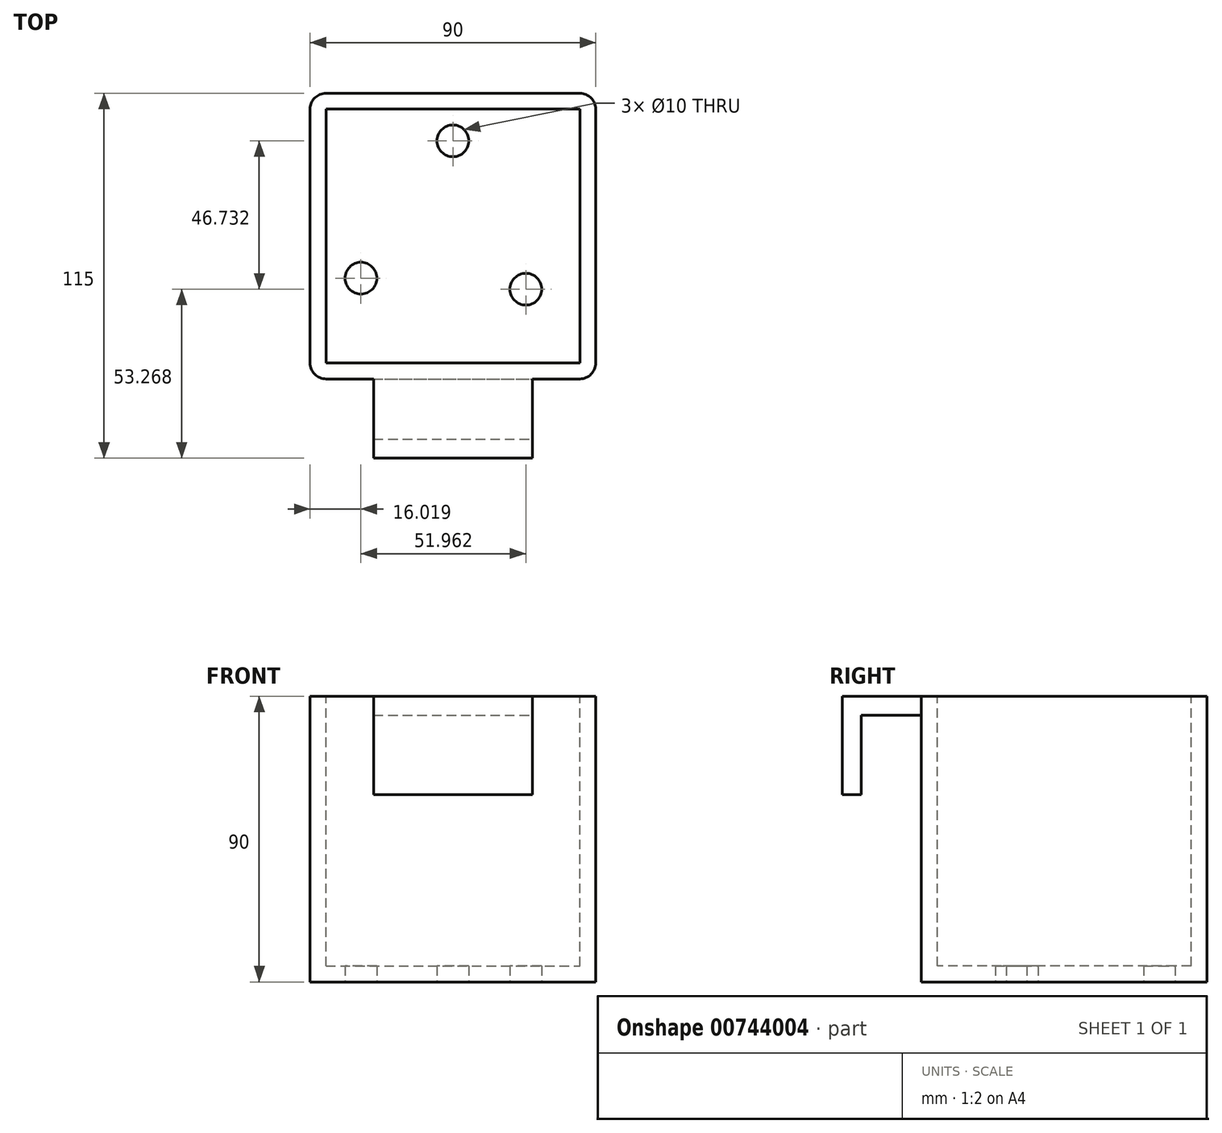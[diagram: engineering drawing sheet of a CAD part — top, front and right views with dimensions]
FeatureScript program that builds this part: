
annotation { "Feature Type Name" : "Feature", "Feature Type Description" : "" }
export const myFeature = defineFeature(function(context is Context, id is Id, definition is map)
    precondition{}
    {
        {
            var Q0;
            Q0=qCreatedBy(makeId("Top.planeOp"),FACE);
            var sketch = newSketch(context, id + "F0", { "sketchPlane" : qUnion([Q0])});
            skLineSegment(sketch, "E0.bottom", {"start": v(0, 0) * mm, "end": v(90, 0) * mm});
            skLineSegment(sketch, "E0.top", {"start": v(0, 90) * mm, "end": v(90, 90) * mm});
            skLineSegment(sketch, "E0.left", {"start": v(0, 0) * mm, "end": v(0, 90) * mm});
            skLineSegment(sketch, "E0.right", {"start": v(90, 0) * mm, "end": v(90, 90) * mm});
            skCircle(sketch, "E1", {"center": v(45, 75) * mm, "radius": 5 * mm});
            skCircle(sketch, "E2.1.0", {"center": v(16.02, 31.73) * mm, "radius": 5 * mm});
            skCircle(sketch, "E2.2.0", {"center": v(67.98, 28.27) * mm, "radius": 5 * mm});
            skPoint(sketch, "E2.center", {"position": v(43, 45) * mm});
            skSolve(sketch);
        }
        {
            var Q0;
            Q0=makeQuery(id+"F0.imprint","IMPRINT",FACE,{"disambiguationData":[TD([[makeQuery(id+"F0.imprint","IMPRINT",EDGE,{"derivedFrom":sQuery(id+"F0.wireOp",EDGE,"E0.bottom")}),1.0]])]});
            extrude(context, id + "F1", {"entities" : qUnion([Q0]), "depth" : 90 * mm, "offsetDistance" : 25 * mm});
        }
        {
            var Q0;
            Q0=makeQuery(id+"F1.opExtrude","SWEPT_EDGE",EDGE,{"disambiguationData":[OSD([sQuery(id+"F0.wireOp",EDGE,"E0.bottom"),sQuery(id+"F0.wireOp",EDGE,"E0.right")])]});
            var Q1;
            Q1=makeQuery(id+"F1.opExtrude","SWEPT_EDGE",EDGE,{"disambiguationData":[OSD([sQuery(id+"F0.wireOp",EDGE,"E0.top"),sQuery(id+"F0.wireOp",EDGE,"E0.right")])]});
            var Q2;
            Q2=makeQuery(id+"F1.opExtrude","SWEPT_EDGE",EDGE,{"disambiguationData":[OSD([sQuery(id+"F0.wireOp",EDGE,"E0.bottom"),sQuery(id+"F0.wireOp",EDGE,"E0.left")])]});
            var Q3;
            Q3=makeQuery(id+"F1.opExtrude","SWEPT_EDGE",EDGE,{"disambiguationData":[OSD([sQuery(id+"F0.wireOp",EDGE,"E0.top"),sQuery(id+"F0.wireOp",EDGE,"E0.left")])]});
            fillet(context, id + "F2", {"entities" : qUnion([Q0, Q1, Q2, Q3]), "radius" : 5 * mm, "tangentPropagation" : true, "allowEdgeOverflow" : false});
        }
        {
            var Q0;
            Q0=makeQuery(id+"F1.opExtrude","CAP_FACE",FACE,{"disambiguationData":[OSD([sQuery(id+"F0.wireOp",EDGE,"E0.bottom"),sQuery(id+"F0.wireOp",EDGE,"E0.top"),sQuery(id+"F0.wireOp",EDGE,"E0.left"),sQuery(id+"F0.wireOp",EDGE,"E0.right"),sQuery(id+"F0.wireOp",EDGE,"E1"),sQuery(id+"F0.wireOp",EDGE,"E2.1.0"),sQuery(id+"F0.wireOp",EDGE,"E2.2.0")])],"isStart":false});
            var sketch = newSketch(context, id + "F3", { "sketchPlane" : qUnion([Q0])});
            skLineSegment(sketch, "E3.bottom", {"start": v(5, 85) * mm, "end": v(85, 85) * mm});
            skLineSegment(sketch, "E3.top", {"start": v(5, 5) * mm, "end": v(85, 5) * mm});
            skLineSegment(sketch, "E3.left", {"start": v(5, 85) * mm, "end": v(5, 5) * mm});
            skLineSegment(sketch, "E3.right", {"start": v(85, 85) * mm, "end": v(85, 5) * mm});
            skSolve(sketch);
        }
        {
            var Q0;
            Q0 = qSketchRegion(id + "F3", true);
            extrude(context, id + "F4", {"entities" : qUnion([Q0]), "operationType" : NewBodyOperationType.REMOVE, "oppositeDirection" : true, "depth" : 85 * mm, "offsetDistance" : 25 * mm});
        }
        {
            var Q0;
            Q0=makeQuery(id+"F1.opExtrude","SWEPT_FACE",FACE,{"disambiguationData":[OSD([sQuery(id+"F0.wireOp",EDGE,"E0.bottom")])]});
            var sketch = newSketch(context, id + "F5", { "sketchPlane" : qUnion([Q0])});
            skLineSegment(sketch, "E4.bottom", {"start": v(20, 90) * mm, "end": v(70, 90) * mm});
            skLineSegment(sketch, "E4.top", {"start": v(20, 84) * mm, "end": v(70, 84) * mm});
            skLineSegment(sketch, "E4.left", {"start": v(20, 90) * mm, "end": v(20, 84) * mm});
            skLineSegment(sketch, "E4.right", {"start": v(70, 90) * mm, "end": v(70, 84) * mm});
            skSolve(sketch);
        }
        {
            var Q0;
            Q0 = qSketchRegion(id + "F5", true);
            extrude(context, id + "F6", {"entities" : qUnion([Q0]), "operationType" : NewBodyOperationType.ADD, "depth" : 25 * mm, "offsetDistance" : 25 * mm});
        }
        {
            var Q0;
            Q0=makeQuery(id+"F6.opExtrude","SWEPT_FACE",FACE,{"disambiguationData":[OSD([sQuery(id+"F5.wireOp",EDGE,"E4.top")])]});
            var sketch = newSketch(context, id + "F7", { "sketchPlane" : qUnion([Q0])});
            skLineSegment(sketch, "E5.bottom", {"start": v(20, 25) * mm, "end": v(70, 25) * mm});
            skLineSegment(sketch, "E5.top", {"start": v(20, 19) * mm, "end": v(70, 19) * mm});
            skLineSegment(sketch, "E5.left", {"start": v(20, 25) * mm, "end": v(20, 19) * mm});
            skLineSegment(sketch, "E5.right", {"start": v(70, 25) * mm, "end": v(70, 19) * mm});
            skSolve(sketch);
        }
        {
            var Q0;
            Q0 = qSketchRegion(id + "F7", true);
            extrude(context, id + "F8", {"entities" : qUnion([Q0]), "operationType" : NewBodyOperationType.ADD, "depth" : 25 * mm, "offsetDistance" : 25 * mm});
        }
    });
